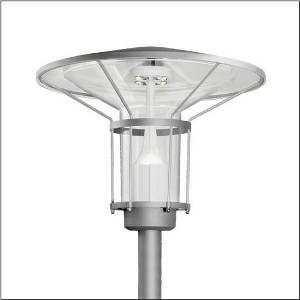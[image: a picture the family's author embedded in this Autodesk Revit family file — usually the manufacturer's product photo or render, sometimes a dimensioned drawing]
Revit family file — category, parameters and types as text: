
# Revit family: laterne_classic_iq___p1_0a_5xa5245lf14h_4a87
name_source: partatom
category: Lighting Fixtures
units: mm (PartAtom-declared; Revit-internal decimal feet)

## family parameters
Cut with Voids When Loaded = No
Host = Face
Light Source = No
Part Type = Normal
Room Calculation Point = No
Round Connector Dimension = Use Diameter
Shared = No

## types (1)
- --- (1 x LED, 1360 lm, 10 W, 4000K)
    Apparent Load = 10 VA
    CIE Flux Codes = 30 61 91 96 100
    Color Rendering = 70
    Color Temperature = 4000K
    Default Elevation = 1800 mm
    Description = Lantern Classic iQ, mast luminaire, Module 540 iQ-SR, primary light control with 3 zone facetted reflector, of plastic, silver coated, highly specular, structured, primary optical cover: cover, of PMMA, transparent, light distribution: P1.0a, light emission: direct distribution, primary light characteristic: strongly asymmetric, installation type: post-top, LED, High Power LED, rated luminous flux: 1.360lm, luminous efficacy: 136lm/W, light colour: 740, colour temperature: 4000K, control gear: ECG iQ, control: presetting dimming logarithmic, Street-Remote, Auto-Match, Temp-Guard, Lumen-Switch, Night-Set, Smart-Wire, Light-Fading, Desk-Remote (wireless, voltage-free reading and setting of iQ features in the workshop via application-optimized NFC function/RFID function), optimised constant luminous flux control (CLO 2.0), with terminal, 6-pole, max. 2.5mm², mains connection: 220..240V, AC, 50/60Hz, start of lifetime: 10W, end of lifetime: 10W, reduction: 5W, luminaire housing, upper part, of glass-fibre reinforced polyester, coated, Siteco® metallic grey (DB 702S), diameter: 750mm, height: 596mm, spigot size: d x l = 76 x 70mm (post-top) | with reducer (optional accessory) 60 x 70mm, post-top mast mounting element, of diecast aluminium, coated, Siteco® metallic grey (DB 702S), Module 540 iQ-SR, traffic white (RAL 9016), equipment: standard, protection rating (complete): IP65, insulation class (complete): insulation class II (safety insulation), certification: CE, ENEC, VDE, packaging unit: 1 piece

Light Distribution: P1.0a
    Height = 596 mm
    Lamp = 1 x LED
    Lamp Light Flux = 1360 lm
    Lamp Power = 10 W
    Lamp count = 1
    Length = 750 mm
    Luminous efficacy = 136 lm/W
    Manufacturer = Siteco
    ModVariant = No
    Model = 5XA5245LF14H
    Number of Poles = 1
    OnlyDefault = Yes
    Power Factor = 1
    Product Name = Laterne Classic iQ | P1.0a
    Product group = mast luminaire | pylon top
    ProductGroupID = 6100
    Protection Class = Protection class II
    Protection Degree = IP 65
    RLX_Detail_Level = 1
    RlxData = <blob elided: 98173 chars, md5=98600a96>
    Socket = socket
    Standby Power = 0 W
    System Light Flux = 1360 lm
    System Power = 10 W
    Type Comments = factory setting: luminous flux: 100 % | dim-lin: 254 | 401 mA
    Type Image = l_1006052.jpg
    URL = http://relux.com
    VarID = @adj_071459
    Voltage = 0 V
    Weight = 0.00 kg
    Width = 0 mm  [stored 0 ft]

note: [stored X ft] marks values corroborated as IEEE doubles in the binary element streams (Revit-internal decimal feet)

## geometry (parser evidence)
native form markers: Blend x4, Sweep x9
no freeform markers — native parametric forms only
